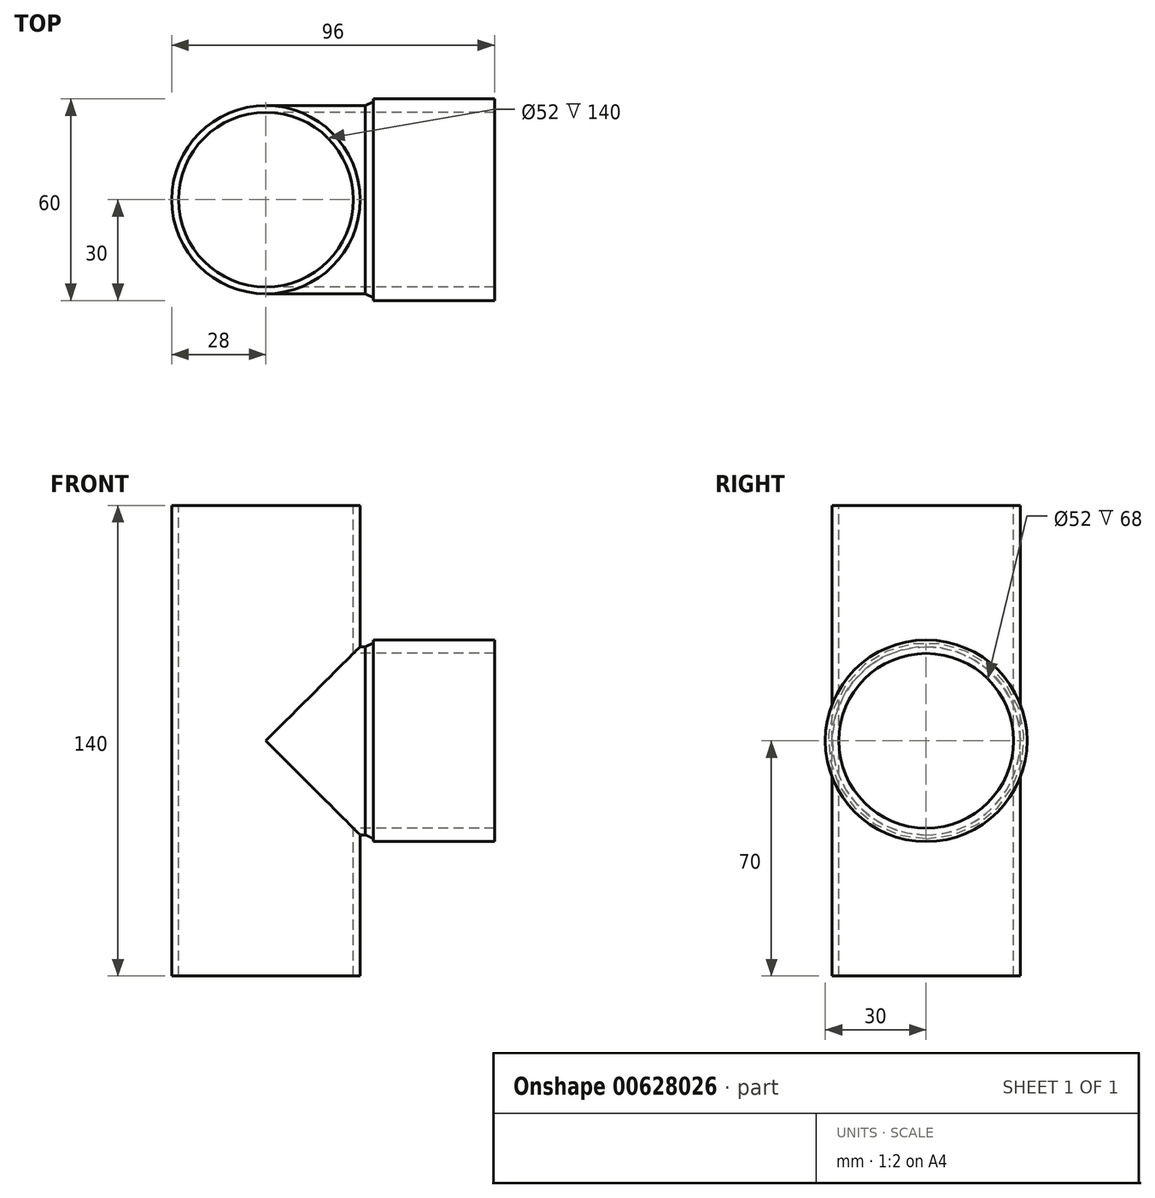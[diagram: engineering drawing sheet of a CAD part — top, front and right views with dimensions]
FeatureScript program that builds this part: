
annotation { "Feature Type Name" : "Feature", "Feature Type Description" : "" }
export const myFeature = defineFeature(function(context is Context, id is Id, definition is map)
    precondition{}
    {
        {
            var Q0;
            Q0=qCreatedBy(makeId("Top.planeOp"),FACE);
            var sketch = newSketch(context, id + "F0", { "sketchPlane" : qUnion([Q0])});
            skCircle(sketch, "E0", {"center": v(0, 0) * mm, "radius": 26 * mm});
            skCircle(sketch, "E1.0", {"center": v(0, 0) * mm, "radius": 28 * mm});
            skSolve(sketch);
        }
        {
            var Q0;
            Q0 = qSketchRegion(id + "F0", true);
            extrude(context, id + "F1", {"entities" : qUnion([Q0]), "oppositeDirection" : true, "depth" : 70 * mm, "offsetDistance" : 25 * mm});
        }
        {
            var Q0;
            Q0=qCreatedBy(makeId("Right.planeOp"),FACE);
            var sketch = newSketch(context, id + "F2", { "sketchPlane" : qUnion([Q0])});
            skCircle(sketch, "E2", {"center": v(0, 0) * mm, "radius": 28 * mm});
            skSolve(sketch);
        }
        {
            var Q0;
            Q0 = qSketchRegion(id + "F2", true);
            extrude(context, id + "F3", {"entities" : qUnion([Q0]), "operationType" : NewBodyOperationType.REMOVE, "depth" : 31 * mm, "offsetDistance" : 25 * mm});
        }
        {
            var Q0;
            Q0=qCreatedBy(makeId("Right.planeOp"),FACE);
            var sketch = newSketch(context, id + "F4", { "sketchPlane" : qUnion([Q0])});
            skCircle(sketch, "E3", {"center": v(0, 0) * mm, "radius": 28 * mm});
            skCircle(sketch, "E4.0", {"center": v(0, 0) * mm, "radius": 26 * mm});
            skSolve(sketch);
        }
        {
            var Q0;
            Q0 = qSketchRegion(id + "F4", true);
            extrude(context, id + "F5", {"entities" : qUnion([Q0]), "depth" : 32 * mm, "offsetDistance" : 25 * mm});
        }
        {
            var Q0;
            Q0=makeQuery(id+"F1.opExtrude","SWEPT_BODY",BODY,{"disambiguationData":[OSD([sQuery(id+"F0.wireOp",EDGE,"E0"),sQuery(id+"F0.wireOp",EDGE,"E1.0")])]});
            var Q1;
            Q1=qCreatedBy(makeId("Top.planeOp"),FACE);
            mirror(context, id + "F6", {"operationType" : NewBodyOperationType.ADD, "entities" : qUnion([Q0]), "mirrorPlane" : qUnion([Q1])});
        }
        {
            var Q0;
            Q0=qCreatedBy(makeId("Top.planeOp"),FACE);
            var sketch = newSketch(context, id + "F7", { "sketchPlane" : qUnion([Q0])});
            skCircle(sketch, "E5", {"center": v(0, 0) * mm, "radius": 26 * mm});
            skSolve(sketch);
        }
        {
            var Q0;
            Q0 = qSketchRegion(id + "F7", true);
            extrude(context, id + "F8", {"entities" : qUnion([Q0]), "operationType" : NewBodyOperationType.REMOVE, "endBound" : BoundingType.SYMMETRIC, "oppositeDirection" : true, "depth" : 150 * mm, "offsetDistance" : 25 * mm});
        }
        {
            var Q0;
            Q0=makeQuery(id+"F5.opExtrude","CAP_FACE",FACE,{"disambiguationData":[OSD([sQuery(id+"F4.wireOp",EDGE,"E3"),sQuery(id+"F4.wireOp",EDGE,"E4.0")])],"isStart":false});
            var sketch = newSketch(context, id + "F9", { "sketchPlane" : qUnion([Q0])});
            skCircle(sketch, "E6.0", {"center": v(0, 0) * mm, "radius": 30 * mm});
            skSolve(sketch);
        }
        {
            var Q0;
            Q0=makeQuery(id+"F9.imprint","IMPRINT",FACE,{"disambiguationData":[TD([[makeQuery(id+"F9.imprint","IMPRINT",EDGE,{"derivedFrom":sQuery(id+"F9.wireOp",EDGE,"E6.0")}),1.0]])]});
            var Q1;
            Q1=makeQuery(id+"F9.imprint","IMPRINT",FACE,{"disambiguationData":[TD([[makeQuery(id+"F9.imprint","IMPRINT",EDGE,{"derivedFrom":makeQuery(id+"F5.opExtrude","CAP_EDGE",EDGE,{"disambiguationData":[OSD([sQuery(id+"F4.wireOp",EDGE,"E3")])],"isStart":false})}),1.0]])]});
            extrude(context, id + "F10", {"entities" : qUnion([Q0, Q1]), "operationType" : NewBodyOperationType.ADD, "depth" : 36 * mm, "offsetDistance" : 25 * mm});
        }
        {
            var Q0;
            Q0=qCreatedBy(makeId("Front.planeOp"),FACE);
            var sketch = newSketch(context, id + "F11", { "sketchPlane" : qUnion([Q0])});
            skLineSegment(sketch, "E7", {"start": v(32, 29.14) * mm, "end": v(29.6, 28) * mm});
            skLineSegment(sketch, "E8", {"start": v(29.6, 28) * mm, "end": v(32, 28) * mm});
            skLineSegment(sketch, "E9", {"start": v(32, 28) * mm, "end": v(32, 29.14) * mm});
            skSolve(sketch);
        }
        {
            var Q0;
            Q0 = qSketchRegion(id + "F11", true);
            var Q1;
            Q1=makeQuery(id+"F10.opExtrude","SWEPT_FACE",FACE,{"disambiguationData":[OSD([sQuery(id+"F9.wireOp",EDGE,"E6.0")])]});
            revolve(context, id + "F12", {"operationType" : NewBodyOperationType.ADD, "entities" : qUnion([Q0]), "axis" : qUnion([Q1]), "revolveType" : RevolveType.FULL});
        }
    });
